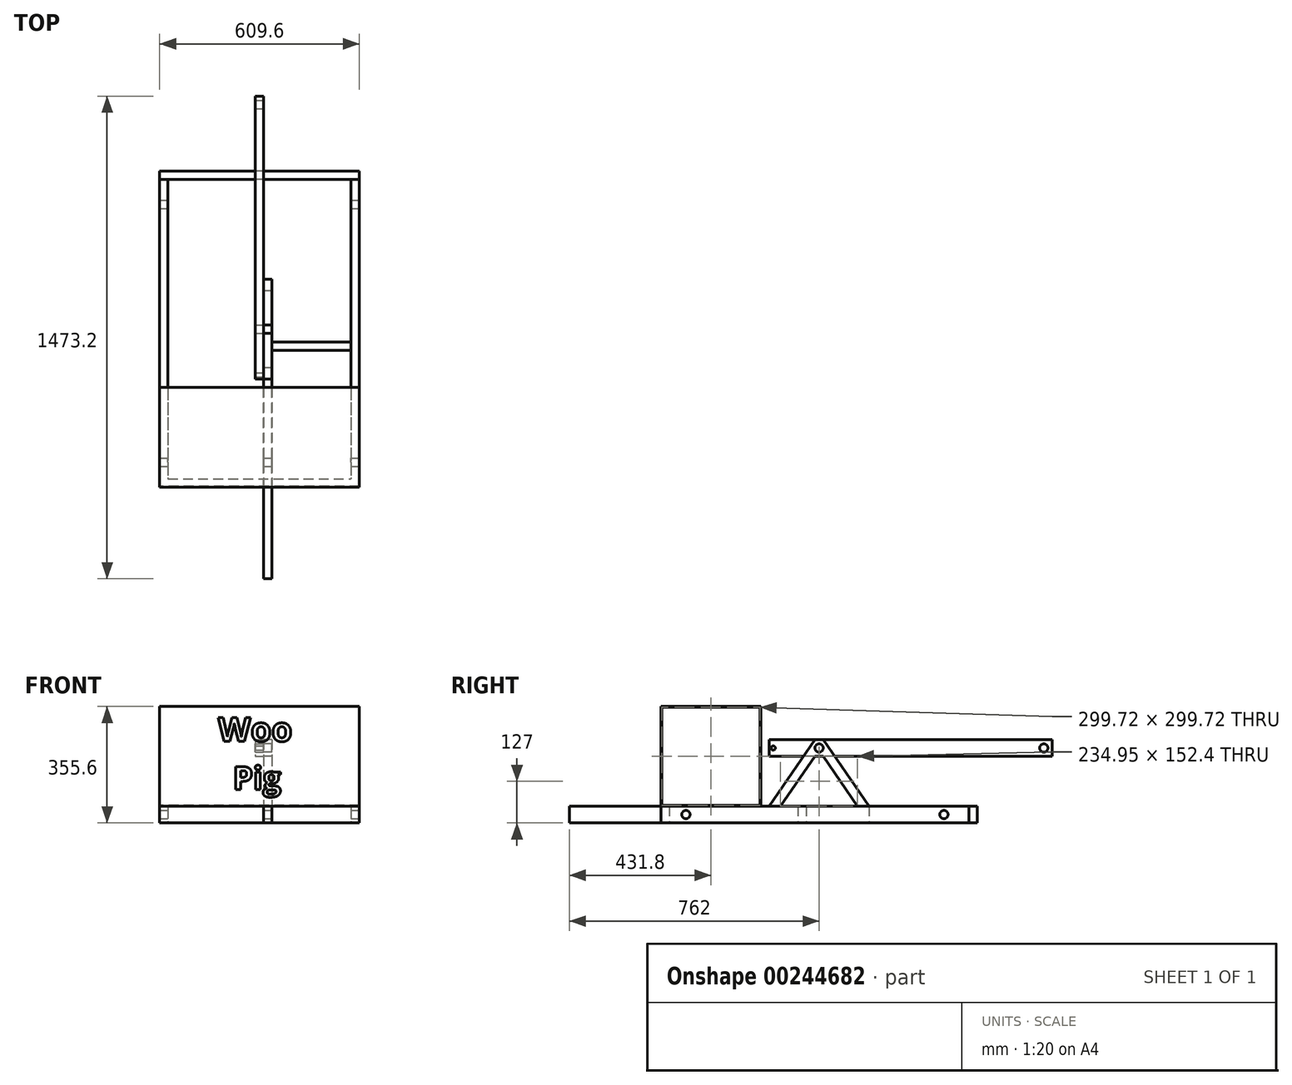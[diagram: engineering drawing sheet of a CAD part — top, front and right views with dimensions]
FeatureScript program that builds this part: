
annotation { "Feature Type Name" : "Feature", "Feature Type Description" : "" }
export const myFeature = defineFeature(function(context is Context, id is Id, definition is map)
    precondition{}
    {
        {
            var Q0;
            Q0=qCreatedBy(makeId("Top.planeOp"),FACE);
            var sketch = newSketch(context, id + "F0", { "sketchPlane" : qUnion([Q0])});
            skLineSegment(sketch, "E0.bottom", {"start": v(0, 863.6) * mm, "end": v(25.4, 863.6) * mm});
            skLineSegment(sketch, "E0.top", {"start": v(0, 0) * mm, "end": v(25.4, 0) * mm});
            skLineSegment(sketch, "E0.left", {"start": v(0, 863.6) * mm, "end": v(0, 0) * mm});
            skLineSegment(sketch, "E0.right", {"start": v(25.4, 863.6) * mm, "end": v(25.4, 0) * mm});
            skSolve(sketch);
        }
        {
            var Q0;
            Q0=makeQuery(id+"F0.imprint","IMPRINT",FACE,{"disambiguationData":[TD([[makeQuery(id+"F0.imprint","IMPRINT",EDGE,{"derivedFrom":sQuery(id+"F0.wireOp",EDGE,"E0.bottom")}),-1.0]])]});
            extrude(context, id + "F1", {"entities" : qUnion([Q0]), "depth" : 50.8 * mm});
        }
        {
            var Q0;
            Q0=makeQuery(id+"F1.opExtrude","SWEPT_FACE",FACE,{"disambiguationData":[OSD([sQuery(id+"F0.wireOp",EDGE,"E0.right")])]});
            var sketch = newSketch(context, id + "F2", { "sketchPlane" : qUnion([Q0])});
            skLineSegment(sketch, "E1", {"start": v(0, 25.4) * mm, "end": v(863.6, 25.4) * mm, "construction": true});
            skCircle(sketch, "E2", {"center": v(152.4, 25.4) * mm, "radius": 12.7 * mm});
            skCircle(sketch, "E3", {"center": v(838.2, 25.4) * mm, "radius": 12.7 * mm});
            skCircle(sketch, "E4", {"center": v(12.7, 25.4) * mm, "radius": 6.35 * mm});
            skSolve(sketch);
        }
        {
            var Q0;
            Q0 = qSketchRegion(id + "F2", true);
            extrude(context, id + "F3", {"entities" : qUnion([Q0]), "operationType" : NewBodyOperationType.REMOVE, "endBound" : BoundingType.THROUGH_ALL, "oppositeDirection" : true, "depth" : 25.4 * mm});
        }
        {
            var Q0;
            Q0=makeQuery(id+"F1.opExtrude","SWEPT_FACE",FACE,{"disambiguationData":[OSD([sQuery(id+"F0.wireOp",EDGE,"E0.right")])]});
            var sketch = newSketch(context, id + "F4", { "sketchPlane" : qUnion([Q0])});
            skLineSegment(sketch, "E5", {"start": v(152.4, 50.8) * mm, "end": v(139.7, 50.8) * mm, "construction": true});
            skLineSegment(sketch, "E6", {"start": v(139.7, 50.8) * mm, "end": v(139.7, 0) * mm, "construction": true});
            skLineSegment(sketch, "E7", {"start": v(165.1, 50.8) * mm, "end": v(165.1, 0) * mm, "construction": true});
            skLineSegment(sketch, "E8", {"start": v(139.7, 50.8) * mm, "end": v(0, -152.4) * mm});
            skLineSegment(sketch, "E9", {"start": v(139.7, 0) * mm, "end": v(34.92, -152.4) * mm});
            skLineSegment(sketch, "E10", {"start": v(139.7, 0) * mm, "end": v(139.7, -152.4) * mm, "construction": true});
            skLineSegment(sketch, "E11", {"start": v(139.7, -152.4) * mm, "end": v(-61.1, -152.4) * mm, "construction": true});
            skLineSegment(sketch, "E12", {"start": v(0, -152.4) * mm, "end": v(-609.6, -152.4) * mm});
            skLineSegment(sketch, "E13", {"start": v(-609.6, -152.4) * mm, "end": v(-609.6, -203.2) * mm});
            skLineSegment(sketch, "E14", {"start": v(-609.6, -203.2) * mm, "end": v(139.7, -203.2) * mm});
            skLineSegment(sketch, "E15", {"start": v(34.92, -152.4) * mm, "end": v(139.7, -152.4) * mm});
            skLineSegment(sketch, "E16", {"start": v(152.4, 50.8) * mm, "end": v(152.4, -203.2) * mm, "construction": true});
            skLineSegment(sketch, "E17", {"start": v(139.7, 50.8) * mm, "end": v(152.4, 50.8) * mm});
            skLineSegment(sketch, "E18.MirrorCS", {"start": v(165.1, 0) * mm, "end": v(269.88, -152.4) * mm});
            skLineSegment(sketch, "E19.MirrorCS", {"start": v(165.1, 50.8) * mm, "end": v(304.8, -152.4) * mm});
            skLineSegment(sketch, "E20.MirrorCS", {"start": v(165.1, -152.4) * mm, "end": v(365.9, -152.4) * mm, "construction": true});
            skLineSegment(sketch, "E21.MirrorCS", {"start": v(152.4, 50.8) * mm, "end": v(165.1, 50.8) * mm, "construction": true});
            skLineSegment(sketch, "E22", {"start": v(139.7, -152.4) * mm, "end": v(269.88, -152.4) * mm});
            skLineSegment(sketch, "E23", {"start": v(139.7, -203.2) * mm, "end": v(165.1, -203.2) * mm});
            skLineSegment(sketch, "E24", {"start": v(139.7, 0) * mm, "end": v(165.1, 0) * mm});
            skLineSegment(sketch, "E25", {"start": v(152.4, 50.8) * mm, "end": v(165.1, 50.8) * mm});
            skLineSegment(sketch, "E26", {"start": v(304.8, -152.4) * mm, "end": v(304.8, -203.2) * mm});
            skLineSegment(sketch, "E27", {"start": v(304.8, -203.2) * mm, "end": v(165.1, -203.2) * mm});
            skLineSegment(sketch, "E28", {"start": v(165.1, -152.4) * mm, "end": v(269.88, -152.4) * mm});
            skSolve(sketch);
        }
        {
            var Q0;
            {var subQ0=sQuery(id+"F4.wireOp",EDGE,"E9");Q0=makeQuery(id+"F4.imprint","IMPRINT",FACE,{"disambiguationData":[TD([[makeQuery(id+"F4.imprint","IMPRINT",EDGE,{"derivedFrom":subQ0}),-1.0]])]});}
            var Q1;
            {var subQ7=sQuery(id+"F4.wireOp",EDGE,"E17");Q1=makeQuery(id+"F4.imprint","IMPRINT",FACE,{"disambiguationData":[TD([[makeQuery(id+"F4.imprint","IMPRINT",EDGE,{"derivedFrom":subQ7}),1.0]])]});}
            extrude(context, id + "F5", {"entities" : qUnion([Q0, Q1]), "depth" : 25.4 * mm});
        }
        {
            var Q0;
            Q0=qCreatedBy(makeId("Front.planeOp"),FACE);
            cPlane(context, id + "F6", {"entities" : qUnion([Q0]), "cplaneType" : CPlaneType.OFFSET, "offset" : 304.8 * mm, "width" : 152.4 * mm, "height" : 152.4 * mm});
        }
        {
            var Q0;
            Q0=qCreatedBy(id+"F6.planeOp",FACE);
            var sketch = newSketch(context, id + "F7", { "sketchPlane" : qUnion([Q0])});
            skLineSegment(sketch, "E29", {"start": v(0, 0) * mm, "end": v(0, -319.22) * mm, "construction": true});
            skLineSegment(sketch, "E30", {"start": v(12.7, 0) * mm, "end": v(12.7, -203.2) * mm, "construction": true});
            skLineSegment(sketch, "E31.bottom", {"start": v(-292.1, -152.4) * mm, "end": v(317.5, -152.4) * mm});
            skLineSegment(sketch, "E31.top", {"start": v(-292.1, -203.2) * mm, "end": v(317.5, -203.2) * mm});
            skLineSegment(sketch, "E31.left", {"start": v(-292.1, -152.4) * mm, "end": v(-292.1, -203.2) * mm});
            skLineSegment(sketch, "E31.right", {"start": v(317.5, -152.4) * mm, "end": v(317.5, -203.2) * mm});
            skLineSegment(sketch, "E32", {"start": v(-27.3, -203.2) * mm, "end": v(60.07, -203.2) * mm, "construction": true});
            skSolve(sketch);
        }
        {
            var Q0;
            Q0=makeQuery(id+"F7.imprint","IMPRINT",FACE,{"disambiguationData":[TD([[makeQuery(id+"F7.imprint","IMPRINT",EDGE,{"derivedFrom":sQuery(id+"F7.wireOp",EDGE,"E31.bottom")}),-1.0]])]});
            extrude(context, id + "F8", {"entities" : qUnion([Q0]), "depth" : 25.4 * mm});
        }
        {
            var Q0;
            Q0=makeQuery(id+"F8.opExtrude","CAP_FACE",FACE,{"disambiguationData":[OSD([sQuery(id+"F7.wireOp",EDGE,"E31.bottom"),sQuery(id+"F7.wireOp",EDGE,"E31.top"),sQuery(id+"F7.wireOp",EDGE,"E31.left"),sQuery(id+"F7.wireOp",EDGE,"E31.right")])],"isStart":true});
            var sketch = newSketch(context, id + "F9", { "sketchPlane" : qUnion([Q0])});
            skLineSegment(sketch, "E33.bottom", {"start": v(-317.5, -152.4) * mm, "end": v(-292.1, -152.4) * mm});
            skLineSegment(sketch, "E33.top", {"start": v(-317.5, -203.2) * mm, "end": v(-292.1, -203.2) * mm});
            skLineSegment(sketch, "E33.left", {"start": v(-317.5, -152.4) * mm, "end": v(-317.5, -203.2) * mm});
            skLineSegment(sketch, "E33.right", {"start": v(-292.1, -152.4) * mm, "end": v(-292.1, -203.2) * mm});
            skSolve(sketch);
        }
        {
            var Q0;
            Q0=makeQuery(id+"F9.imprint","IMPRINT",FACE,{"disambiguationData":[TD([[makeQuery(id+"F9.imprint","IMPRINT",EDGE,{"derivedFrom":sQuery(id+"F9.wireOp",EDGE,"E33.bottom")}),1.0]])]});
            extrude(context, id + "F10", {"entities" : qUnion([Q0]), "operationType" : NewBodyOperationType.ADD, "depth" : 914.4 * mm});
        }
        {
            var Q0;
            Q0=makeQuery(id+"F8.opExtrude","CAP_FACE",FACE,{"disambiguationData":[OSD([sQuery(id+"F7.wireOp",EDGE,"E31.bottom"),sQuery(id+"F7.wireOp",EDGE,"E31.top"),sQuery(id+"F7.wireOp",EDGE,"E31.left"),sQuery(id+"F7.wireOp",EDGE,"E31.right")])],"isStart":true});
            var sketch = newSketch(context, id + "F11", { "sketchPlane" : qUnion([Q0])});
            skLineSegment(sketch, "E34.bottom", {"start": v(292.1, -152.4) * mm, "end": v(266.7, -152.4) * mm});
            skLineSegment(sketch, "E34.top", {"start": v(292.1, -203.2) * mm, "end": v(266.7, -203.2) * mm});
            skLineSegment(sketch, "E34.left", {"start": v(292.1, -152.4) * mm, "end": v(292.1, -203.2) * mm});
            skLineSegment(sketch, "E34.right", {"start": v(266.7, -152.4) * mm, "end": v(266.7, -203.2) * mm});
            skSolve(sketch);
        }
        {
            var Q0;
            Q0=makeQuery(id+"F11.imprint","IMPRINT",FACE,{"disambiguationData":[TD([[makeQuery(id+"F11.imprint","IMPRINT",EDGE,{"derivedFrom":sQuery(id+"F11.wireOp",EDGE,"E34.bottom")}),1.0]])]});
            extrude(context, id + "F12", {"entities" : qUnion([Q0]), "operationType" : NewBodyOperationType.ADD, "depth" : 914.4 * mm});
        }
        {
            var Q0;
            Q0=makeQuery(id+"F10.opExtrude","CAP_FACE",FACE,{"disambiguationData":[OSD([sQuery(id+"F9.wireOp",EDGE,"E33.bottom"),sQuery(id+"F9.wireOp",EDGE,"E33.top"),sQuery(id+"F9.wireOp",EDGE,"E33.left"),sQuery(id+"F9.wireOp",EDGE,"E33.right")])],"isStart":false});
            var sketch = newSketch(context, id + "F13", { "sketchPlane" : qUnion([Q0])});
            skLineSegment(sketch, "E35.bottom", {"start": v(-317.5, -152.4) * mm, "end": v(292.1, -152.4) * mm});
            skLineSegment(sketch, "E35.top", {"start": v(-317.5, -203.2) * mm, "end": v(292.1, -203.2) * mm});
            skLineSegment(sketch, "E35.left", {"start": v(-317.5, -152.4) * mm, "end": v(-317.5, -203.2) * mm});
            skLineSegment(sketch, "E35.right", {"start": v(292.1, -152.4) * mm, "end": v(292.1, -203.2) * mm});
            skSolve(sketch);
        }
        {
            var Q0;
            Q0 = qSketchRegion(id + "F13", true);
            extrude(context, id + "F14", {"entities" : qUnion([Q0]), "depth" : 25.4 * mm});
        }
        {
            var Q0;
            Q0=makeQuery(id+"F10.boolean.opBoolean","MERGE",FACE,{"derivedFrom":[makeQuery(id+"F8.opExtrude","SWEPT_FACE",FACE,{"disambiguationData":[OSD([sQuery(id+"F7.wireOp",EDGE,"E31.right")])]}),makeQuery(id+"F10.opExtrude","SWEPT_FACE",FACE,{"disambiguationData":[OSD([sQuery(id+"F9.wireOp",EDGE,"E33.left")])]})]});
            var sketch = newSketch(context, id + "F15", { "sketchPlane" : qUnion([Q0])});
            skLineSegment(sketch, "E36.bottom", {"start": v(-330.2, -152.4) * mm, "end": v(609.6, -152.4) * mm, "construction": true});
            skLineSegment(sketch, "E36.top", {"start": v(-330.2, -203.2) * mm, "end": v(609.6, -203.2) * mm, "construction": true});
            skLineSegment(sketch, "E36.left", {"start": v(-330.2, -152.4) * mm, "end": v(-330.2, -203.2) * mm, "construction": true});
            skLineSegment(sketch, "E36.right", {"start": v(609.6, -152.4) * mm, "end": v(609.6, -203.2) * mm, "construction": true});
            skLineSegment(sketch, "E37", {"start": v(609.6, -177.8) * mm, "end": v(-330.2, -177.8) * mm, "construction": true});
            skCircle(sketch, "E38", {"center": v(-254, -177.8) * mm, "radius": 12.7 * mm});
            skLineSegment(sketch, "E39", {"start": v(139.7, -152.4) * mm, "end": v(139.7, -203.2) * mm, "construction": true});
            skCircle(sketch, "E40.MirrorC", {"center": v(533.4, -177.8) * mm, "radius": 12.7 * mm});
            skSolve(sketch);
        }
        {
            var Q0;
            Q0 = qSketchRegion(id + "F15", true);
            extrude(context, id + "F16", {"entities" : qUnion([Q0]), "operationType" : NewBodyOperationType.REMOVE, "endBound" : BoundingType.THROUGH_ALL, "oppositeDirection" : true, "depth" : 25.4 * mm});
        }
        {
            var Q0;
            Q0=makeQuery(id+"F12.boolean.opBoolean","MERGE",FACE,{"derivedFrom":[makeQuery(id+"F10.boolean.opBoolean","MERGE",FACE,{"derivedFrom":[makeQuery(id+"F8.opExtrude","SWEPT_FACE",FACE,{"disambiguationData":[OSD([sQuery(id+"F7.wireOp",EDGE,"E31.top")])]}),makeQuery(id+"F10.opExtrude","SWEPT_FACE",FACE,{"disambiguationData":[OSD([sQuery(id+"F9.wireOp",EDGE,"E33.top")])]})]}),makeQuery(id+"F12.opExtrude","SWEPT_FACE",FACE,{"disambiguationData":[OSD([sQuery(id+"F11.wireOp",EDGE,"E34.top")])]})]});
            var sketch = newSketch(context, id + "F17", { "sketchPlane" : qUnion([Q0])});
            skLineSegment(sketch, "E41.bottom", {"start": v(292.1, -87.93) * mm, "end": v(50.8, -87.93) * mm});
            skLineSegment(sketch, "E41.top", {"start": v(292.1, -113.33) * mm, "end": v(50.8, -113.33) * mm});
            skLineSegment(sketch, "E41.left", {"start": v(292.1, -87.93) * mm, "end": v(292.1, -113.33) * mm});
            skLineSegment(sketch, "E41.right", {"start": v(50.8, -87.93) * mm, "end": v(50.8, -113.33) * mm});
            skSolve(sketch);
        }
        {
            var Q0;
            Q0=makeQuery(id+"F17.imprint","IMPRINT",FACE,{"disambiguationData":[TD([[makeQuery(id+"F17.imprint","IMPRINT",EDGE,{"derivedFrom":sQuery(id+"F17.wireOp",EDGE,"E41.bottom")}),1.0]])]});
            extrude(context, id + "F18", {"entities" : qUnion([Q0]), "oppositeDirection" : true, "depth" : 50.8 * mm});
        }
        {
            var Q0;
            Q0=makeQuery(id+"F12.boolean.opBoolean","MERGE",FACE,{"derivedFrom":[makeQuery(id+"F8.opExtrude","SWEPT_FACE",FACE,{"disambiguationData":[OSD([sQuery(id+"F7.wireOp",EDGE,"E31.left")])]}),makeQuery(id+"F12.opExtrude","SWEPT_FACE",FACE,{"disambiguationData":[OSD([sQuery(id+"F11.wireOp",EDGE,"E34.left")])]})]});
            var sketch = newSketch(context, id + "F19", { "sketchPlane" : qUnion([Q0])});
            skLineSegment(sketch, "E42.bottom", {"start": v(330.2, -152.4) * mm, "end": v(25.4, -152.4) * mm});
            skLineSegment(sketch, "E42.top", {"start": v(330.2, 152.4) * mm, "end": v(25.4, 152.4) * mm});
            skLineSegment(sketch, "E42.left", {"start": v(330.2, -152.4) * mm, "end": v(330.2, 152.4) * mm});
            skLineSegment(sketch, "E42.right", {"start": v(25.4, -152.4) * mm, "end": v(25.4, 152.4) * mm});
            skSolve(sketch);
        }
        {
            var Q0;
            Q0=makeQuery(id+"F19.imprint","IMPRINT",FACE,{"disambiguationData":[TD([[makeQuery(id+"F19.imprint","IMPRINT",EDGE,{"derivedFrom":sQuery(id+"F19.wireOp",EDGE,"E42.bottom")}),-1.0]])]});
            extrude(context, id + "F20", {"entities" : qUnion([Q0]), "oppositeDirection" : true, "depth" : 609.6 * mm});
        }
        {
            var Q0;
            Q0=makeQuery(id+"F20.opExtrude","CAP_FACE",FACE,{"disambiguationData":[OSD([sQuery(id+"F19.wireOp",EDGE,"E42.bottom"),sQuery(id+"F19.wireOp",EDGE,"E42.top"),sQuery(id+"F19.wireOp",EDGE,"E42.left"),sQuery(id+"F19.wireOp",EDGE,"E42.right")])],"isStart":true});
            var Q1;
            Q1=makeQuery(id+"F20.opExtrude","CAP_FACE",FACE,{"disambiguationData":[OSD([sQuery(id+"F19.wireOp",EDGE,"E42.bottom"),sQuery(id+"F19.wireOp",EDGE,"E42.top"),sQuery(id+"F19.wireOp",EDGE,"E42.left"),sQuery(id+"F19.wireOp",EDGE,"E42.right")])],"isStart":false});
            shell(context, id + "F21", {"entities" : qUnion([Q0, Q1]), "thickness" : 2.54 * mm});
        }
        {
            var Q0;
            Q0=makeQuery(id+"F20.opExtrude","SWEPT_FACE",FACE,{"disambiguationData":[OSD([sQuery(id+"F19.wireOp",EDGE,"E42.left")])]});
            var sketch = newSketch(context, id + "F22", { "sketchPlane" : qUnion([Q0])});
            skText(sketch, "E43", { "text": "Woo", "fontName": "OpenSans-Bold.ttf"});
            skText(sketch, "E44", { "text": "Pig", "fontName": "OpenSans-Bold.ttf"});
            const initialGuessF22  = {"E43": [-0.1139, 0.04534, 1, 0, 0.07397], "E44": [-0.06886, -0.1016, 1, 0, 0.07074]};
            skSetInitialGuess(sketch, initialGuessF22);
            skSolve(sketch);
        }
        {
            var Q0;
            Q0 = qSketchRegion(id + "F22", true);
            extrude(context, id + "F23", {"entities" : qUnion([Q0]), "operationType" : NewBodyOperationType.REMOVE, "oppositeDirection" : true, "depth" : 1.27 * mm});
        }
        {
            var Q0;
            Q0=makeQuery(id+"F5.opExtrude","SWEPT_BODY",BODY,{"disambiguationData":[OSD([sQuery(id+"F2.wireOp",EDGE,"E2"),sQuery(id+"F4.wireOp",EDGE,"E8"),sQuery(id+"F4.wireOp",EDGE,"E9"),sQuery(id+"F4.wireOp",EDGE,"E12"),sQuery(id+"F4.wireOp",EDGE,"E13"),sQuery(id+"F4.wireOp",EDGE,"E14"),sQuery(id+"F4.wireOp",EDGE,"E15"),sQuery(id+"F4.wireOp",EDGE,"E17"),sQuery(id+"F4.wireOp",EDGE,"E18.MirrorCS"),sQuery(id+"F4.wireOp",EDGE,"E19.MirrorCS"),sQuery(id+"F4.wireOp",EDGE,"E22"),sQuery(id+"F4.wireOp",EDGE,"E23"),sQuery(id+"F4.wireOp",EDGE,"E24"),sQuery(id+"F4.wireOp",EDGE,"E25"),sQuery(id+"F4.wireOp",EDGE,"E26"),sQuery(id+"F4.wireOp",EDGE,"E27"),sQuery(id+"F4.wireOp",EDGE,"E28")])]});
            transform(context, id + "F24", {"entities" : qUnion([Q0]), "transformType" : TransformType.TRANSLATION_3D, "dx" : 0 * mm, "dy" : 0 * mm, "dz" : 0 * mm, "makeCopy" : true});
        }
        {
            var Q0;
            Q0=makeQuery(id+"F24.opPattern","COPY",BODY,{"derivedFrom":makeQuery(id+"F5.opExtrude","SWEPT_BODY",BODY,{"disambiguationData":[OSD([sQuery(id+"F2.wireOp",EDGE,"E2"),sQuery(id+"F4.wireOp",EDGE,"E8"),sQuery(id+"F4.wireOp",EDGE,"E9"),sQuery(id+"F4.wireOp",EDGE,"E12"),sQuery(id+"F4.wireOp",EDGE,"E13"),sQuery(id+"F4.wireOp",EDGE,"E14"),sQuery(id+"F4.wireOp",EDGE,"E15"),sQuery(id+"F4.wireOp",EDGE,"E17"),sQuery(id+"F4.wireOp",EDGE,"E18.MirrorCS"),sQuery(id+"F4.wireOp",EDGE,"E19.MirrorCS"),sQuery(id+"F4.wireOp",EDGE,"E22"),sQuery(id+"F4.wireOp",EDGE,"E23"),sQuery(id+"F4.wireOp",EDGE,"E24"),sQuery(id+"F4.wireOp",EDGE,"E25"),sQuery(id+"F4.wireOp",EDGE,"E26"),sQuery(id+"F4.wireOp",EDGE,"E27"),sQuery(id+"F4.wireOp",EDGE,"E28")])]}),"instanceName":"1"});
            deleteBodies(context, id + "F25", {"entities" : qUnion([Q0])});
        }
    });
